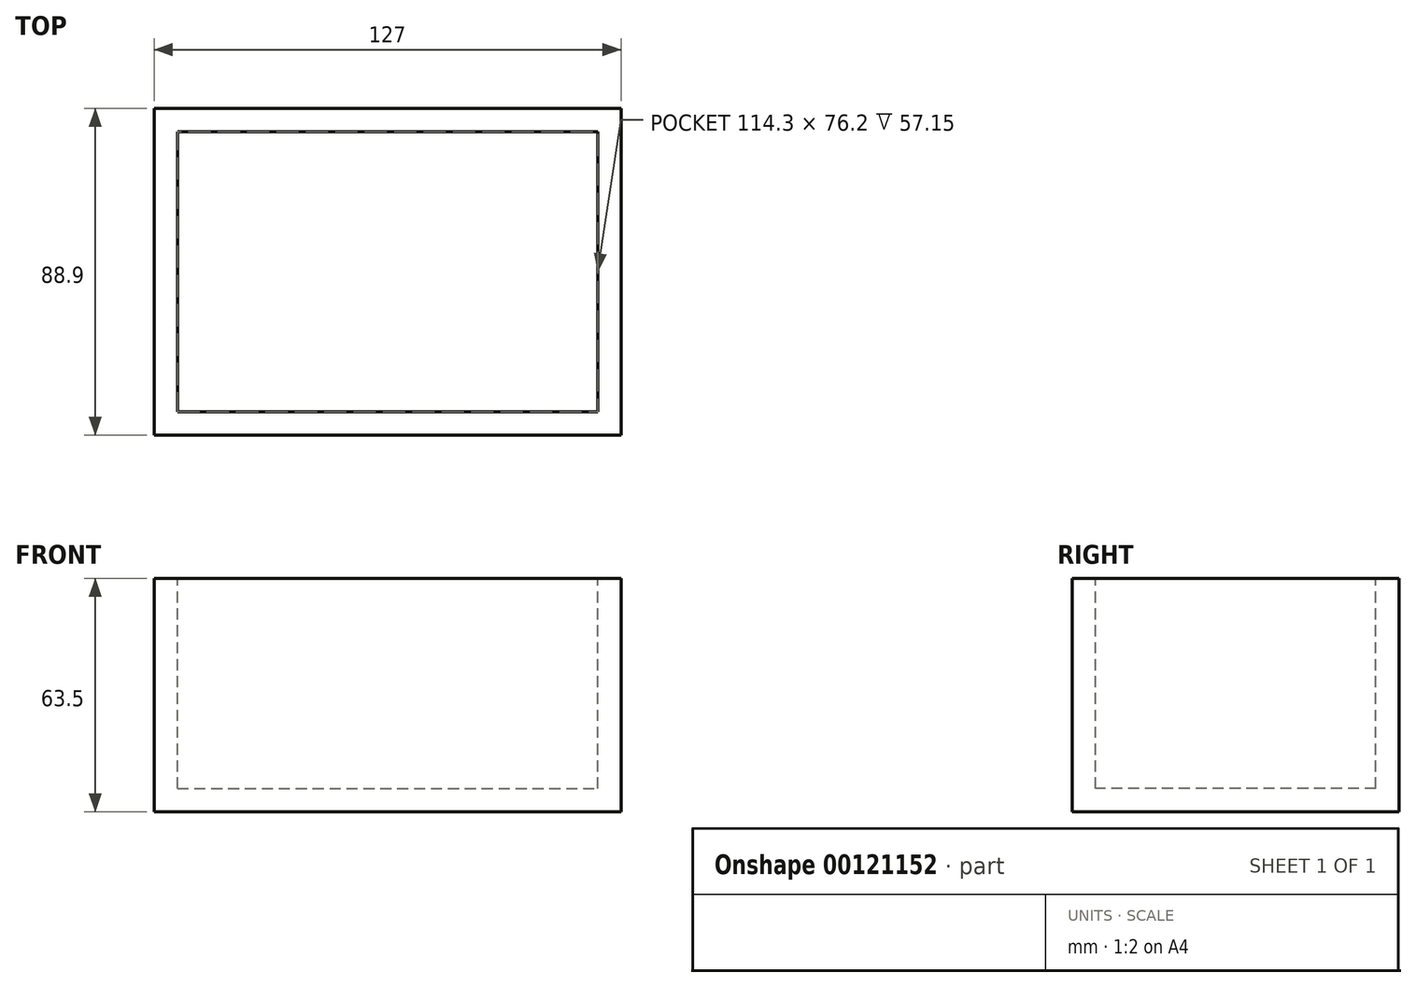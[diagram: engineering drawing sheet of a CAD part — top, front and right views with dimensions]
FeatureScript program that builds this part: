
annotation { "Feature Type Name" : "Feature", "Feature Type Description" : "" }
export const myFeature = defineFeature(function(context is Context, id is Id, definition is map)
    precondition{}
    {
        {
            var Q0;
            Q0=qCreatedBy(makeId("Front.planeOp"),FACE);
            var sketch = newSketch(context, id + "F0", { "sketchPlane" : qUnion([Q0])});
            skLineSegment(sketch, "E0.bottom", {"start": v(-59.9, 43.97) * mm, "end": v(67.1, 43.97) * mm});
            skLineSegment(sketch, "E0.top", {"start": v(-59.9, -19.53) * mm, "end": v(67.1, -19.53) * mm});
            skLineSegment(sketch, "E0.left", {"start": v(-59.9, 43.97) * mm, "end": v(-59.9, -19.53) * mm});
            skLineSegment(sketch, "E0.right", {"start": v(67.1, 43.97) * mm, "end": v(67.1, -19.53) * mm});
            skSolve(sketch);
        }
        {
            var Q0;
            Q0=makeQuery(id+"F0.imprint","IMPRINT",FACE,{"disambiguationData":[TD([[makeQuery(id+"F0.imprint","IMPRINT",EDGE,{"derivedFrom":sQuery(id+"F0.wireOp",EDGE,"E0.bottom")}),-1.0]])]});
            extrude(context, id + "F1", {"entities" : qUnion([Q0]), "depth" : 88.9 * mm});
        }
        {
            var Q0;
            Q0=makeQuery(id+"F1.opExtrude","SWEPT_FACE",FACE,{"disambiguationData":[OSD([sQuery(id+"F0.wireOp",EDGE,"E0.bottom")])]});
            var sketch = newSketch(context, id + "F2", { "sketchPlane" : qUnion([Q0])});
            skLineSegment(sketch, "E1.bottom", {"start": v(-53.54, -6.35) * mm, "end": v(60.76, -6.35) * mm});
            skLineSegment(sketch, "E1.top", {"start": v(-53.54, -82.55) * mm, "end": v(60.76, -82.55) * mm});
            skLineSegment(sketch, "E1.left", {"start": v(-53.54, -6.35) * mm, "end": v(-53.54, -82.55) * mm});
            skLineSegment(sketch, "E1.right", {"start": v(60.76, -6.35) * mm, "end": v(60.76, -82.55) * mm});
            skLineSegment(sketch, "E2.bottom", {"start": v(-59.9, 0) * mm, "end": v(67.1, 0) * mm});
            skLineSegment(sketch, "E2.top", {"start": v(-59.9, -88.9) * mm, "end": v(67.1, -88.9) * mm});
            skLineSegment(sketch, "E2.left", {"start": v(-59.9, 0) * mm, "end": v(-59.9, -88.9) * mm});
            skLineSegment(sketch, "E2.right", {"start": v(67.1, 0) * mm, "end": v(67.1, -88.9) * mm});
            skSolve(sketch);
        }
        {
            var Q0;
            Q0=makeQuery(id+"F2.imprint","IMPRINT",FACE,{"disambiguationData":[TD([[makeQuery(id+"F2.imprint","IMPRINT",EDGE,{"derivedFrom":sQuery(id+"F2.wireOp",EDGE,"E1.bottom")}),-1.0]])]});
            extrude(context, id + "F3", {"entities" : qUnion([Q0]), "operationType" : NewBodyOperationType.REMOVE, "oppositeDirection" : true, "depth" : 57.15 * mm});
        }
    });
